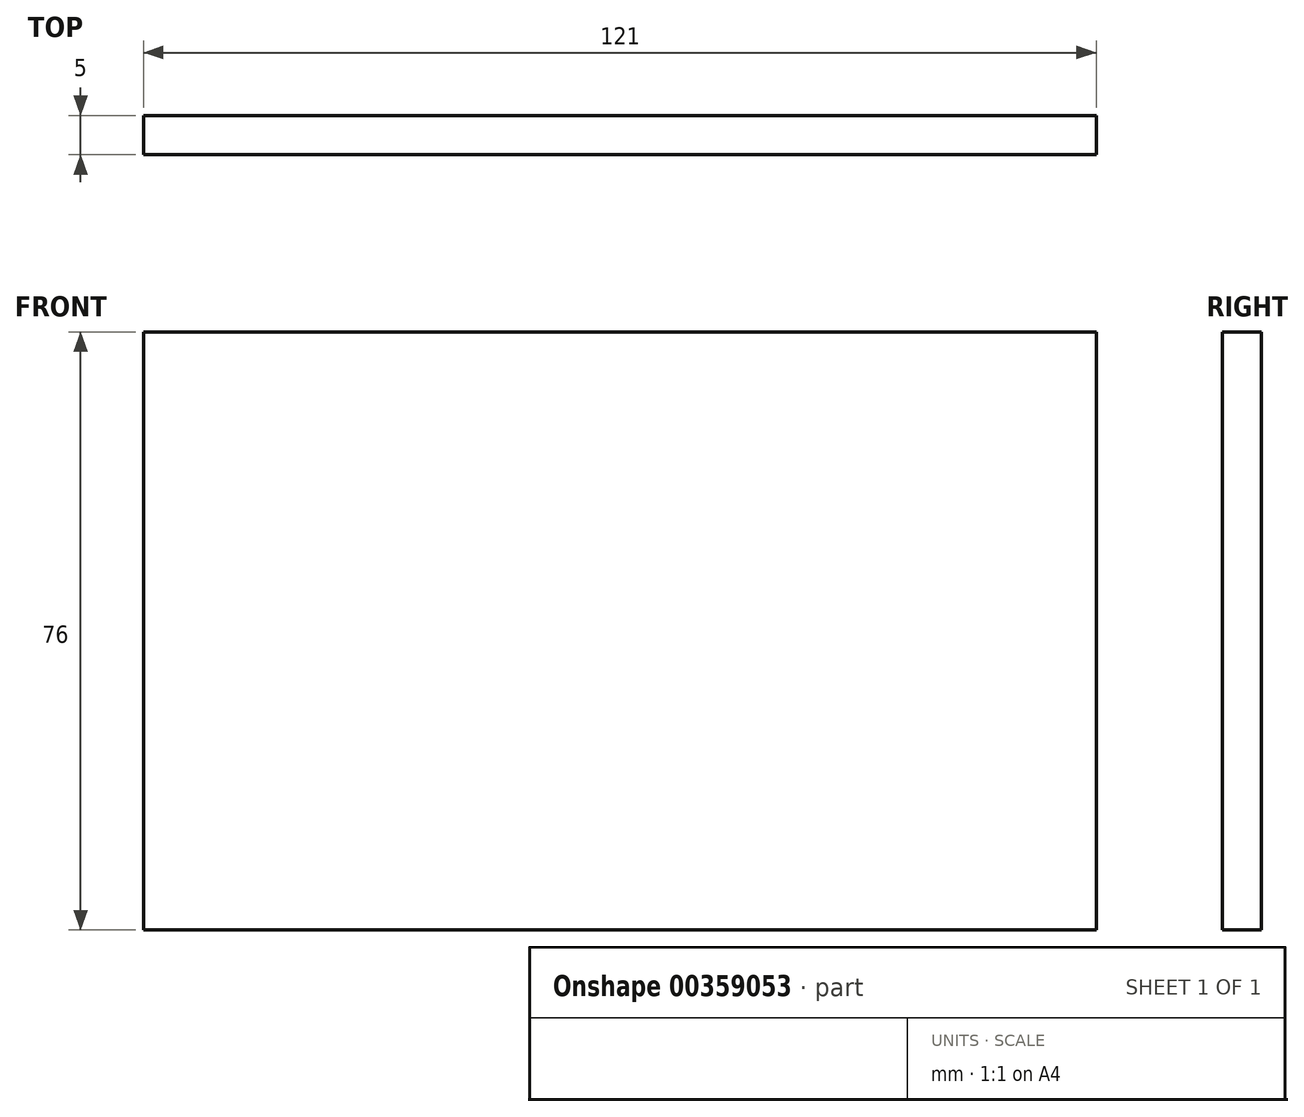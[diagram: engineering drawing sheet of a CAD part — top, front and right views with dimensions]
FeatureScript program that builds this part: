
annotation { "Feature Type Name" : "Feature", "Feature Type Description" : "" }
export const myFeature = defineFeature(function(context is Context, id is Id, definition is map)
    precondition{}
    {
        {
            var Q0;
            Q0=qCreatedBy(makeId("Front.planeOp"),FACE);
            var sketch = newSketch(context, id + "F0", { "sketchPlane" : qUnion([Q0])});
            skLineSegment(sketch, "E0.bottom", {"start": v(-60.5, 38) * mm, "end": v(60.5, 38) * mm});
            skLineSegment(sketch, "E0.top", {"start": v(-60.5, -38) * mm, "end": v(60.5, -38) * mm});
            skLineSegment(sketch, "E0.left", {"start": v(-60.5, 38) * mm, "end": v(-60.5, -38) * mm});
            skLineSegment(sketch, "E0.right", {"start": v(60.5, 38) * mm, "end": v(60.5, -38) * mm});
            skSolve(sketch);
        }
        {
            var Q0;
            Q0 = qSketchRegion(id + "F0", true);
            extrude(context, id + "F1", {"entities" : qUnion([Q0]), "depth" : 5 * mm, "offsetDistance" : 25 * mm});
        }
    });
